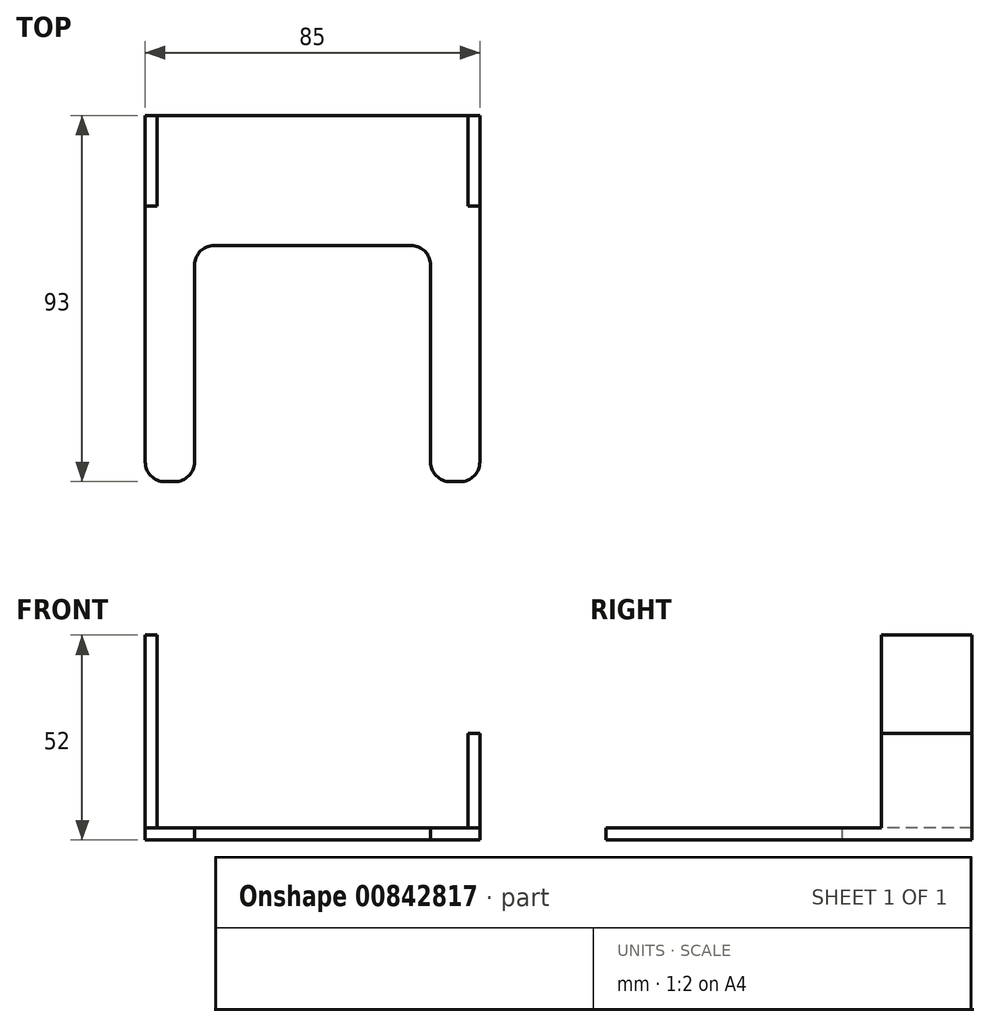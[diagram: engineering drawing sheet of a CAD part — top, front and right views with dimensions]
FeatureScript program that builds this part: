
annotation { "Feature Type Name" : "Feature", "Feature Type Description" : "" }
export const myFeature = defineFeature(function(context is Context, id is Id, definition is map)
    precondition{}
    {
        {
            var Q0;
            Q0=qCreatedBy(makeId("Top.planeOp"),FACE);
            var sketch = newSketch(context, id + "F0", { "sketchPlane" : qUnion([Q0])});
            skLineSegment(sketch, "E0.bottom", {"start": v(0, 0) * mm, "end": v(85, 0) * mm});
            skLineSegment(sketch, "E0.top", {"start": v(0, 23) * mm, "end": v(85, 23) * mm});
            skLineSegment(sketch, "E0.left", {"start": v(0, 0) * mm, "end": v(0, 23) * mm});
            skLineSegment(sketch, "E0.right", {"start": v(85, 0) * mm, "end": v(85, 23) * mm});
            skLineSegment(sketch, "E1.top", {"start": v(17.5, -10) * mm, "end": v(67.5, -10) * mm});
            skLineSegment(sketch, "E1.left", {"start": v(0, 0) * mm, "end": v(0, -10) * mm});
            skLineSegment(sketch, "E1.right", {"start": v(85, 0) * mm, "end": v(85, -10) * mm});
            skLineSegment(sketch, "E2.top", {"start": v(5, -70) * mm, "end": v(7.5, -70) * mm});
            skLineSegment(sketch, "E2.left", {"start": v(0, -10) * mm, "end": v(0, -65) * mm});
            skLineSegment(sketch, "E2.right", {"start": v(12.5, -15) * mm, "end": v(12.5, -65) * mm});
            skLineSegment(sketch, "E3.top", {"start": v(80, -70) * mm, "end": v(77.5, -70) * mm});
            skLineSegment(sketch, "E3.left", {"start": v(85, -10) * mm, "end": v(85, -65) * mm});
            skLineSegment(sketch, "E3.right", {"start": v(72.5, -15) * mm, "end": v(72.5, -65) * mm});
            skPoint(sketch, "E4.visualSharp", {"position": v(12.5, -70) * mm});
            skArc(sketch, "E4.filletArc", {"start": v(7.5, -70) * mm, "mid": v(11.04, -68.54) * mm, "end": v(12.5, -65) * mm});
            skPoint(sketch, "E5.visualSharp", {"position": v(0, -70) * mm});
            skArc(sketch, "E5.filletArc", {"start": v(0, -65) * mm, "mid": v(1.46, -68.54) * mm, "end": v(5, -70) * mm});
            skPoint(sketch, "E6.visualSharp", {"position": v(72.5, -70) * mm});
            skArc(sketch, "E6.filletArc", {"start": v(72.5, -65) * mm, "mid": v(73.96, -68.54) * mm, "end": v(77.5, -70) * mm});
            skPoint(sketch, "E7.visualSharp", {"position": v(85, -70) * mm});
            skArc(sketch, "E7.filletArc", {"start": v(80, -70) * mm, "mid": v(83.54, -68.54) * mm, "end": v(85, -65) * mm});
            skPoint(sketch, "E8.visualSharp", {"position": v(12.5, -10) * mm});
            skArc(sketch, "E8.filletArc", {"start": v(17.5, -10) * mm, "mid": v(13.96, -11.46) * mm, "end": v(12.5, -15) * mm});
            skPoint(sketch, "E9.visualSharp", {"position": v(72.5, -10) * mm});
            skArc(sketch, "E9.filletArc", {"start": v(72.5, -15) * mm, "mid": v(71.04, -11.46) * mm, "end": v(67.5, -10) * mm});
            skSolve(sketch);
        }
        {
            var Q0;
            Q0=qSketchRegion(id+"F0",true);
            extrude(context, id + "F1", {"entities" : qUnion([Q0]), "depth" : 3 * mm, "offsetDistance" : 25 * mm});
        }
        {
            var Q0;
            Q0=makeQuery(id+"F1.opExtrude","CAP_FACE",FACE,{"disambiguationData":[OSD([sQuery(id+"F0.wireOp",EDGE,"E0.bottom"),sQuery(id+"F0.wireOp",EDGE,"E0.top"),sQuery(id+"F0.wireOp",EDGE,"E0.left"),sQuery(id+"F0.wireOp",EDGE,"E0.right")])],"isStart":false});
            var sketch = newSketch(context, id + "F2", { "sketchPlane" : qUnion([Q0])});
            skLineSegment(sketch, "E10.bottom", {"start": v(0, 23) * mm, "end": v(3, 23) * mm});
            skLineSegment(sketch, "E10.top", {"start": v(0, 0) * mm, "end": v(3, 0) * mm});
            skLineSegment(sketch, "E10.left", {"start": v(0, 23) * mm, "end": v(0, 0) * mm});
            skLineSegment(sketch, "E10.right", {"start": v(3, 23) * mm, "end": v(3, 0) * mm});
            skLineSegment(sketch, "E11.bottom", {"start": v(85, 23) * mm, "end": v(82, 23) * mm});
            skLineSegment(sketch, "E11.top", {"start": v(85, 0) * mm, "end": v(82, 0) * mm});
            skLineSegment(sketch, "E11.left", {"start": v(85, 23) * mm, "end": v(85, 0) * mm});
            skLineSegment(sketch, "E11.right", {"start": v(82, 23) * mm, "end": v(82, 0) * mm});
            skSolve(sketch);
        }
        {
            var Q0;
            Q0=qSketchRegion(id+"F2",true);
            extrude(context, id + "F3", {"entities" : qUnion([Q0]), "operationType" : NewBodyOperationType.ADD, "depth" : 24 * mm, "offsetDistance" : 25 * mm});
        }
        {
            var Q0;
            Q0=makeQuery(id+"F3.opExtrude","CAP_FACE",FACE,{"disambiguationData":[OSD([sQuery(id+"F2.wireOp",EDGE,"E10.bottom"),sQuery(id+"F2.wireOp",EDGE,"E10.top"),sQuery(id+"F2.wireOp",EDGE,"E10.left"),sQuery(id+"F2.wireOp",EDGE,"E10.right")])],"isStart":false});
            var sketch = newSketch(context, id + "F4", { "sketchPlane" : qUnion([Q0])});
            skLineSegment(sketch, "E12.bottom", {"start": v(0, 23) * mm, "end": v(3, 23) * mm});
            skLineSegment(sketch, "E12.top", {"start": v(0, 0) * mm, "end": v(3, 0) * mm});
            skLineSegment(sketch, "E12.left", {"start": v(0, 23) * mm, "end": v(0, 0) * mm});
            skLineSegment(sketch, "E12.right", {"start": v(3, 23) * mm, "end": v(3, 0) * mm});
            skSolve(sketch);
        }
        {
            var Q0;
            Q0=qSketchRegion(id+"F4",true);
            extrude(context, id + "F5", {"entities" : qUnion([Q0]), "operationType" : NewBodyOperationType.ADD, "depth" : 25 * mm, "offsetDistance" : 25 * mm});
        }
    });
